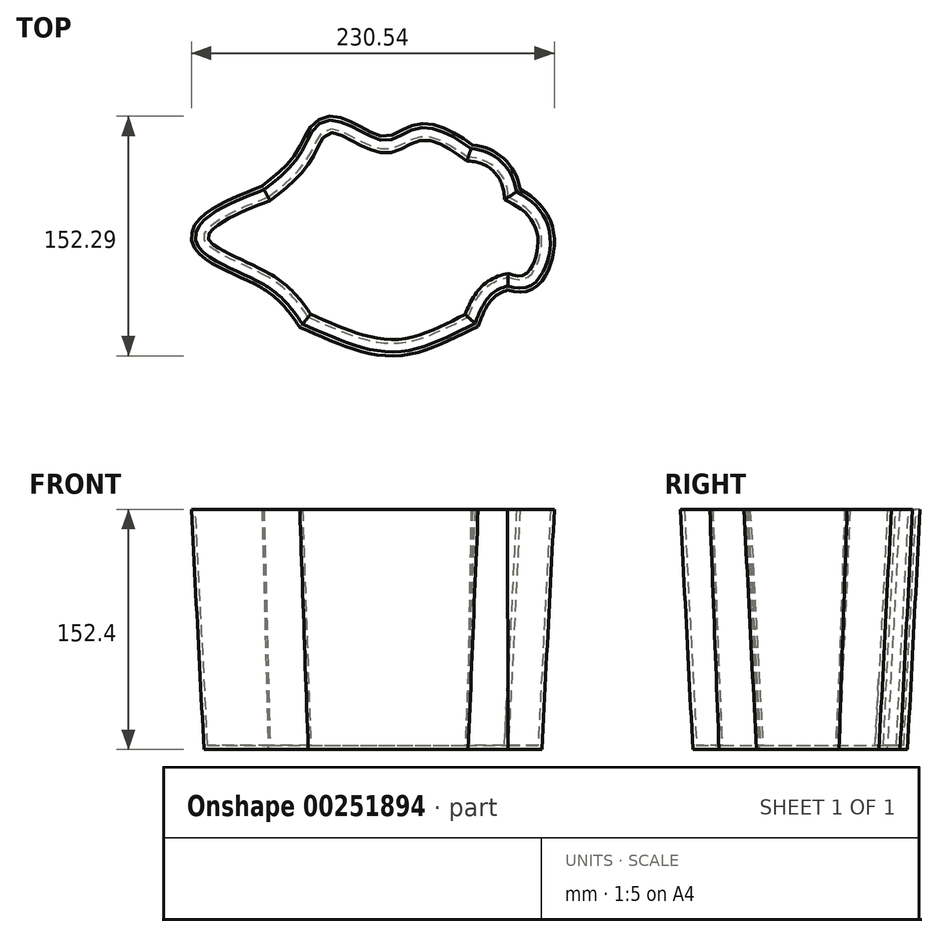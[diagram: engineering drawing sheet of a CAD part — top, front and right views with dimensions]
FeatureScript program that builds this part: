
annotation { "Feature Type Name" : "Feature", "Feature Type Description" : "" }
export const myFeature = defineFeature(function(context is Context, id is Id, definition is map)
    precondition{}
    {
        {
            var Q0;
            Q0=qCreatedBy(makeId("Top.planeOp"),FACE);
            var sketch = newSketch(context, id + "F0", { "sketchPlane" : qUnion([Q0])});
            skPoint(sketch, "E0.visualSharp", {"position": v(-76.65, 51.93) * mm});
            skPoint(sketch, "E1.visualSharp", {"position": v(75.75, 51.93) * mm});
            skArc(sketch, "E1.filletArc", {"start": v(75.75, 26.53) * mm, "mid": v(68.31, 44.49) * mm, "end": v(50.35, 51.93) * mm});
            skPoint(sketch, "E2.visualSharp", {"position": v(75.75, -49.67) * mm});
            skPoint(sketch, "E3.visualSharp", {"position": v(-76.65, -49.67) * mm});
            skArc(sketch, "E3.filletArc", {"start": v(-76.65, -24.27) * mm, "mid": v(-69.21, -42.23) * mm, "end": v(-51.25, -49.67) * mm});
            skFitSpline(sketch, "E4", {"points": [v(-51.25, -49.67) * mm, v(3.17, -66.25) * mm, v(50.35, -49.67) * mm], "startDerivative": vector(106.85, -45.54) * mm, "endDerivative": vector(96.25, 46.44) * mm});
            skFitSpline(sketch, "E5", {"points": [v(50.35, -49.67) * mm, v(61.28, -31.26) * mm, v(75.75, -24.27) * mm], "startDerivative": vector(16, 42.7) * mm, "endDerivative": vector(35.35, 7.1) * mm});
            skFitSpline(sketch, "E6", {"points": [v(75.75, -24.27) * mm, v(88.26, -24.27) * mm, v(96.86, 2.53) * mm, v(75.75, 26.53) * mm], "startDerivative": vector(50.6, -17.36) * mm, "endDerivative": vector(-91.4, 40.78) * mm});
            skFitSpline(sketch, "E7", {"points": [v(-51.25, -49.67) * mm, v(-76.65, -24.27) * mm, v(-117.29, 0) * mm, v(-76.65, 26.53) * mm], "startDerivative": vector(-60.89, 89.16) * mm, "endDerivative": vector(195.65, 72.6) * mm});
            skFitSpline(sketch, "E8", {"points": [v(-76.65, 26.53) * mm, v(-51.25, 51.93) * mm, v(-37.69, 70) * mm, v(-3.57, 57.15) * mm, v(20.38, 65.18) * mm, v(50.35, 51.93) * mm], "startDerivative": vector(135.72, 103.97) * mm, "endDerivative": vector(147.85, -107.17) * mm});
            skSolve(sketch);
        }
        {
            var Q0;
            Q0=makeQuery(id+"F0.imprint","IMPRINT",FACE,{"disambiguationData":[TD([[makeQuery(id+"F0.imprint","IMPRINT",EDGE,{"derivedFrom":sQuery(id+"F0.wireOp",EDGE,"E1.filletArc")}),1.0]])]});
            extrude(context, id + "F1", {"entities" : qUnion([Q0]), "depth" : 152.4 * mm, "hasDraft" : true, "draftAngle" : 3 * degree});
        }
        {
            var Q0;
            Q0=makeQuery(id+"F1.opExtrude","CAP_FACE",FACE,{"disambiguationData":[OSD([sQuery(id+"F0.wireOp",EDGE,"E1.filletArc"),sQuery(id+"F0.wireOp",EDGE,"E3.filletArc"),sQuery(id+"F0.wireOp",EDGE,"E4"),sQuery(id+"F0.wireOp",EDGE,"E5"),sQuery(id+"F0.wireOp",EDGE,"E6"),sQuery(id+"F0.wireOp",EDGE,"E7"),sQuery(id+"F0.wireOp",EDGE,"E8")])],"isStart":false});
            shell(context, id + "F2", {"entities" : qUnion([Q0]), "thickness" : 2.54 * mm});
        }
    });
